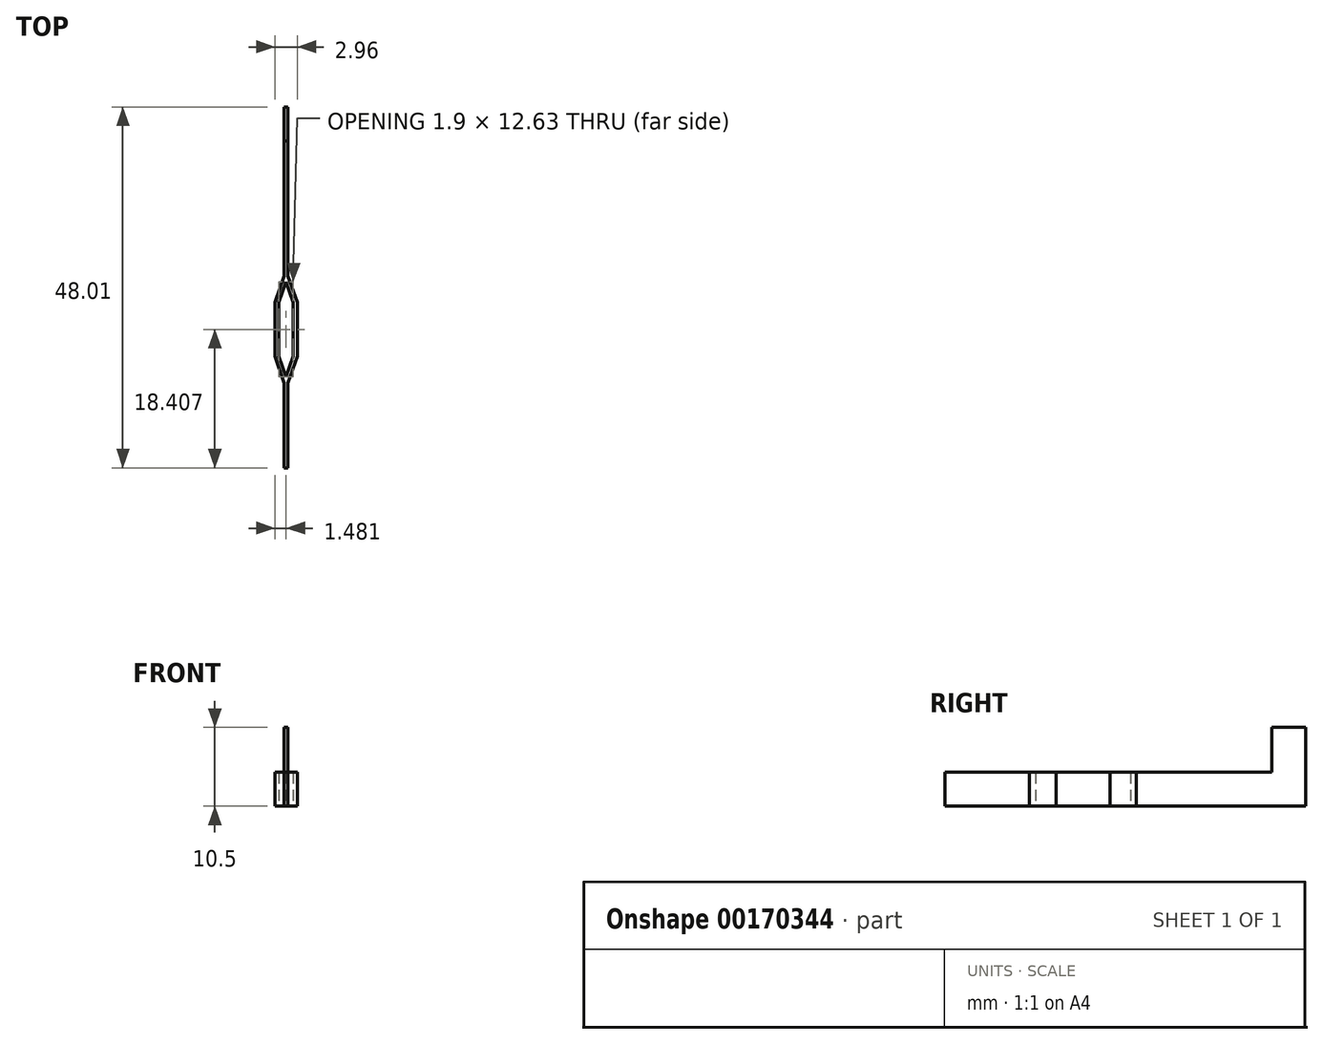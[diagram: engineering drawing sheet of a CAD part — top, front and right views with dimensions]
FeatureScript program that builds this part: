
annotation { "Feature Type Name" : "Feature", "Feature Type Description" : "" }
export const myFeature = defineFeature(function(context is Context, id is Id, definition is map)
    precondition{}
    {
        {
            var Q0;
            Q0=qCreatedBy(makeId("Top.planeOp"),FACE);
            var sketch = newSketch(context, id + "F0", { "sketchPlane" : qUnion([Q0])});
            skLineSegment(sketch, "E0.bottom", {"start": v(-0.97, 31.3) * mm, "end": v(-0.47, 31.3) * mm});
            skLineSegment(sketch, "E0.top", {"start": v(-0.97, -16.7) * mm, "end": v(-0.47, -16.7) * mm});
            skLineSegment(sketch, "E1.bottom", {"start": v(-1.67, 5.3) * mm, "end": v(0.23, 5.3) * mm});
            skLineSegment(sketch, "E1.top", {"start": v(-1.67, -1.9) * mm, "end": v(0.23, -1.9) * mm});
            skLineSegment(sketch, "E1.left", {"start": v(-1.67, 5.3) * mm, "end": v(-1.67, -1.9) * mm});
            skLineSegment(sketch, "E1.right", {"start": v(0.23, 5.3) * mm, "end": v(0.23, -1.9) * mm});
            skLineSegment(sketch, "E2", {"start": v(-1.67, 5.3) * mm, "end": v(-0.97, 7.3) * mm});
            skLineSegment(sketch, "E3", {"start": v(-0.47, 7.3) * mm, "end": v(0.23, 5.3) * mm});
            skLineSegment(sketch, "E4", {"start": v(-1.67, -1.9) * mm, "end": v(-0.97, -3.9) * mm});
            skLineSegment(sketch, "E5", {"start": v(-0.47, -3.9) * mm, "end": v(0.23, -1.9) * mm});
            skLineSegment(sketch, "E6", {"start": v(-0.97, 8.82) * mm, "end": v(-2.2, 5.3) * mm});
            skLineSegment(sketch, "E7", {"start": v(-2.2, 5.3) * mm, "end": v(-2.2, -1.9) * mm});
            skLineSegment(sketch, "E8", {"start": v(-2.2, -1.9) * mm, "end": v(-0.97, -5.4) * mm});
            skLineSegment(sketch, "E9", {"start": v(-0.47, 8.82) * mm, "end": v(0.76, 5.3) * mm});
            skLineSegment(sketch, "E10", {"start": v(0.76, 5.3) * mm, "end": v(0.76, -1.9) * mm});
            skLineSegment(sketch, "E11", {"start": v(0.76, -1.9) * mm, "end": v(-0.47, -5.4) * mm});
            skLineSegment(sketch, "E12", {"start": v(-0.97, 31.3) * mm, "end": v(-0.97, 8.82) * mm});
            skLineSegment(sketch, "E13", {"start": v(-0.97, -5.4) * mm, "end": v(-0.97, -16.7) * mm});
            skLineSegment(sketch, "E14", {"start": v(-0.47, 31.3) * mm, "end": v(-0.47, 8.82) * mm});
            skLineSegment(sketch, "E15", {"start": v(-0.47, -5.4) * mm, "end": v(-0.47, -16.7) * mm});
            skLineSegment(sketch, "E16", {"start": v(-0.47, 7.3) * mm, "end": v(-0.72, 8.02) * mm});
            skLineSegment(sketch, "E17", {"start": v(-0.72, 8.02) * mm, "end": v(-0.97, 7.3) * mm});
            skLineSegment(sketch, "E18", {"start": v(-0.47, -3.9) * mm, "end": v(-0.72, -4.6) * mm});
            skLineSegment(sketch, "E19", {"start": v(-0.97, -3.9) * mm, "end": v(-0.72, -4.6) * mm});
            skSolve(sketch);
        }
        {
            var Q0;
            Q0=makeQuery(id+"F0.imprint","IMPRINT",FACE,{"disambiguationData":[TD([[makeQuery(id+"F0.imprint","IMPRINT",EDGE,{"derivedFrom":sQuery(id+"F0.wireOp",EDGE,"E0.bottom")}),-1.0]])]});
            var Q1;
            Q1=sQuery(id+"F0.wireOp",EDGE,"E3");
            var Q2;
            Q2=sQuery(id+"F0.wireOp",EDGE,"E1.right");
            var Q3;
            Q3=sQuery(id+"F0.wireOp",EDGE,"E5");
            var Q4;
            Q4=sQuery(id+"F0.wireOp",EDGE,"nkD4Ib0B-5Y8a-obz0-IcfC-dqy6glZyB51n");
            var Q5;
            Q5=sQuery(id+"F0.wireOp",EDGE,"diSldYqd-0EJK-Tftk-uqzO-esxdoyUf5riP");
            var Q6;
            Q6=sQuery(id+"F0.wireOp",EDGE,"E1.left");
            var Q7;
            Q7=sQuery(id+"F0.wireOp",EDGE,"E2");
            var Q8;
            Q8=sQuery(id+"F0.wireOp",EDGE,"E4");
            var Q9;
            Q9=sQuery(id+"F0.wireOp",EDGE,"E8");
            var Q10;
            Q10=sQuery(id+"F0.wireOp",EDGE,"E7");
            var Q11;
            Q11=sQuery(id+"F0.wireOp",EDGE,"E10");
            var Q12;
            Q12=sQuery(id+"F0.wireOp",EDGE,"E11");
            var Q13;
            Q13=sQuery(id+"F0.wireOp",EDGE,"E14");
            var Q14;
            Q14=sQuery(id+"F0.wireOp",EDGE,"E12");
            var Q15;
            Q15=sQuery(id+"F0.wireOp",EDGE,"E6");
            var Q16;
            Q16=sQuery(id+"F0.wireOp",EDGE,"E9");
            var Q17;
            Q17=sQuery(id+"F0.wireOp",EDGE,"E0.bottom");
            var Q18;
            Q18=sQuery(id+"F0.wireOp",EDGE,"E15");
            var Q19;
            Q19=sQuery(id+"F0.wireOp",EDGE,"E13");
            var Q20;
            Q20=sQuery(id+"F0.wireOp",EDGE,"E0.top");
            extrude(context, id + "F1", {"entities" : qUnion([Q0]), "surfaceEntities" : qUnion([Q1, Q2, Q3, Q4, Q5, Q6, Q7, Q8, Q9, Q10, Q11, Q12, Q13, Q14, Q15, Q16, Q17, Q18, Q19, Q20]), "depth" : 4.5 * mm});
        }
        {
            var Q0;
            Q0=makeQuery(id+"F1.opExtrude","CAP_FACE",FACE,{"disambiguationData":[OSD([sQuery(id+"F0.wireOp",EDGE,"E0.bottom"),sQuery(id+"F0.wireOp",EDGE,"E0.top"),sQuery(id+"F0.wireOp",EDGE,"E1.left"),sQuery(id+"F0.wireOp",EDGE,"E1.right"),sQuery(id+"F0.wireOp",EDGE,"E2"),sQuery(id+"F0.wireOp",EDGE,"E3"),sQuery(id+"F0.wireOp",EDGE,"E4"),sQuery(id+"F0.wireOp",EDGE,"E5"),sQuery(id+"F0.wireOp",EDGE,"E6"),sQuery(id+"F0.wireOp",EDGE,"E7"),sQuery(id+"F0.wireOp",EDGE,"E8"),sQuery(id+"F0.wireOp",EDGE,"E9"),sQuery(id+"F0.wireOp",EDGE,"E10"),sQuery(id+"F0.wireOp",EDGE,"E11"),sQuery(id+"F0.wireOp",EDGE,"E12"),sQuery(id+"F0.wireOp",EDGE,"E13"),sQuery(id+"F0.wireOp",EDGE,"E14"),sQuery(id+"F0.wireOp",EDGE,"E15"),sQuery(id+"F0.wireOp",EDGE,"E16"),sQuery(id+"F0.wireOp",EDGE,"E17"),sQuery(id+"F0.wireOp",EDGE,"E18"),sQuery(id+"F0.wireOp",EDGE,"E19")])],"isStart":false});
            var sketch = newSketch(context, id + "F2", { "sketchPlane" : qUnion([Q0])});
            skLineSegment(sketch, "E20.bottom", {"start": v(-0.97, 31.3) * mm, "end": v(-0.47, 31.3) * mm});
            skLineSegment(sketch, "E20.top", {"start": v(-0.97, 26.8) * mm, "end": v(-0.47, 26.8) * mm});
            skLineSegment(sketch, "E20.left", {"start": v(-0.97, 31.3) * mm, "end": v(-0.97, 26.8) * mm});
            skLineSegment(sketch, "E20.right", {"start": v(-0.47, 31.3) * mm, "end": v(-0.47, 26.8) * mm});
            skSolve(sketch);
        }
        {
            var Q0;
            Q0=makeQuery(id+"F2.imprint","IMPRINT",FACE,{"disambiguationData":[TD([[makeQuery(id+"F2.imprint","IMPRINT",EDGE,{"derivedFrom":sQuery(id+"F2.wireOp",EDGE,"E20.bottom")}),-1.0]])]});
            extrude(context, id + "F3", {"entities" : qUnion([Q0]), "operationType" : NewBodyOperationType.ADD, "depth" : 6 * mm});
        }
    });
